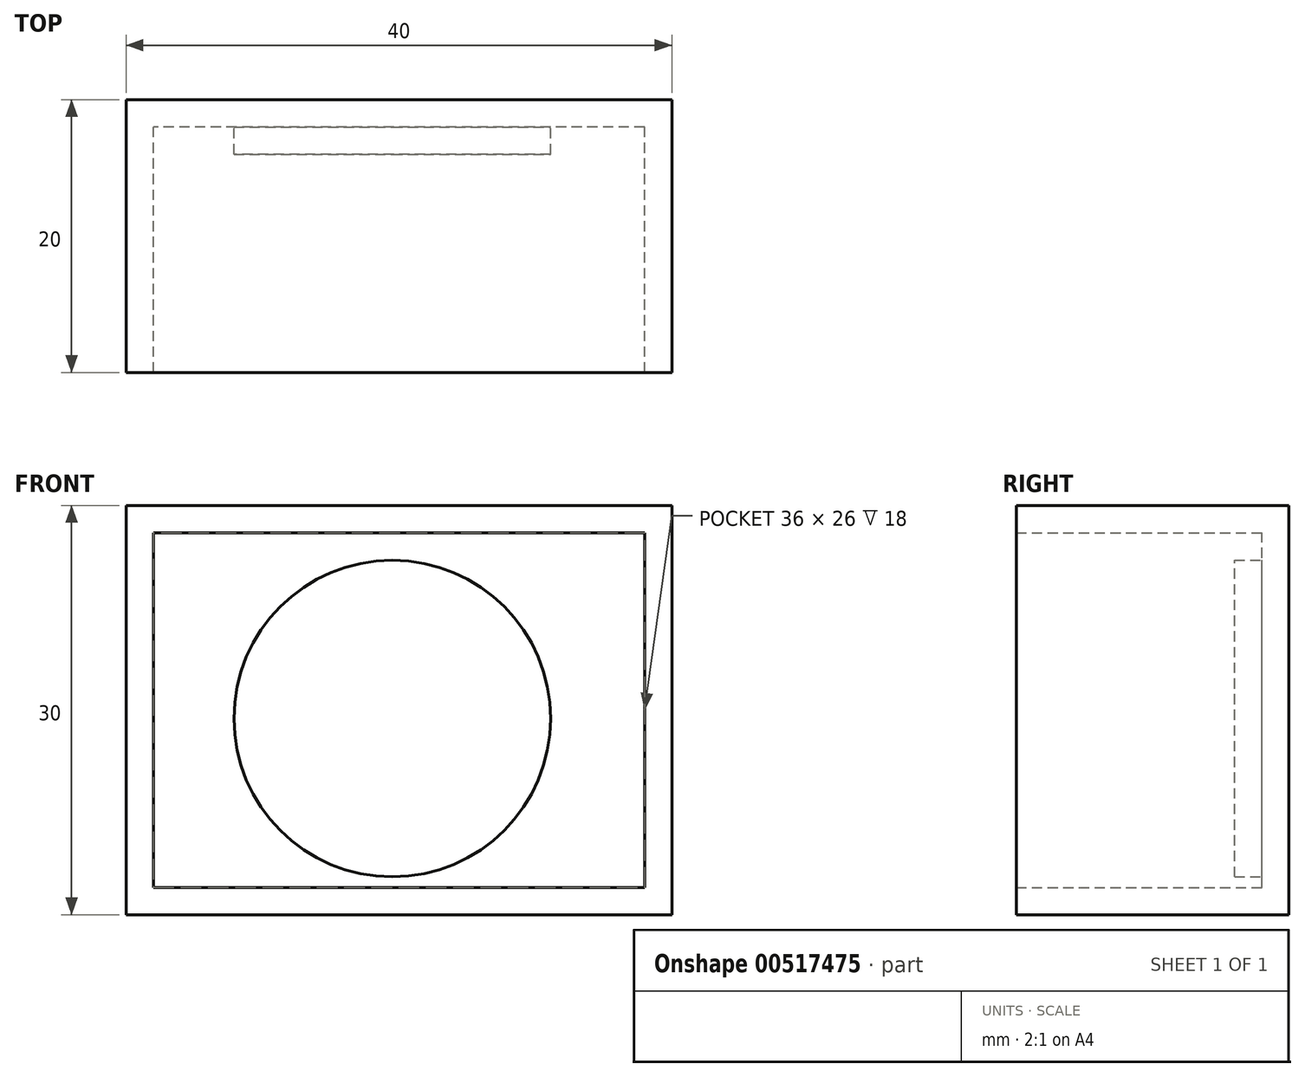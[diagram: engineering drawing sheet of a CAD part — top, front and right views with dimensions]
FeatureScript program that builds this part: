
annotation { "Feature Type Name" : "Feature", "Feature Type Description" : "" }
export const myFeature = defineFeature(function(context is Context, id is Id, definition is map)
    precondition{}
    {
        {
            var Q0;
            Q0=qCreatedBy(makeId("Front.planeOp"),FACE);
            var sketch = newSketch(context, id + "F0", { "sketchPlane" : qUnion([Q0])});
            skLineSegment(sketch, "E0.bottom", {"start": v(0, 0) * mm, "end": v(-40, 0) * mm});
            skLineSegment(sketch, "E0.top", {"start": v(0, 30) * mm, "end": v(-40, 30) * mm});
            skLineSegment(sketch, "E0.left", {"start": v(0, 0) * mm, "end": v(0, 30) * mm});
            skLineSegment(sketch, "E0.right", {"start": v(-40, 0) * mm, "end": v(-40, 30) * mm});
            skSolve(sketch);
        }
        {
            var Q0;
            Q0 = qSketchRegion(id + "F0", true);
            var Q1;
            Q1=makeQuery(id+"F0.imprint","IMPRINT",FACE,{"disambiguationData":[TD([[makeQuery(id+"F0.imprint","IMPRINT",EDGE,{"derivedFrom":sQuery(id+"F0.wireOp",EDGE,"E0.bottom")}),-1.0]])]});
            extrude(context, id + "F1", {"entities" : qUnion([Q0, Q1]), "depth" : 20 * mm, "offsetDistance" : 25.4 * mm});
        }
        {
            var Q0;
            Q0=makeQuery(id+"F1.opExtrude","CAP_FACE",FACE,{"disambiguationData":[OSD([sQuery(id+"F0.wireOp",EDGE,"E0.bottom"),sQuery(id+"F0.wireOp",EDGE,"E0.top"),sQuery(id+"F0.wireOp",EDGE,"E0.left"),sQuery(id+"F0.wireOp",EDGE,"E0.right")])],"isStart":false});
            shell(context, id + "F2", {"entities" : qUnion([Q0]), "thickness" : 2 * mm});
        }
        {
            var Q0;
            Q0=makeQuery(id+"F2.opShell","OFFSET_FACE",FACE,{"disambiguationData":[OSD([sQuery(id+"F0.wireOp",EDGE,"E0.bottom"),sQuery(id+"F0.wireOp",EDGE,"E0.top"),sQuery(id+"F0.wireOp",EDGE,"E0.left"),sQuery(id+"F0.wireOp",EDGE,"E0.right")])]});
            var sketch = newSketch(context, id + "F3", { "sketchPlane" : qUnion([Q0])});
            skCircle(sketch, "E1", {"center": v(-20.5, 14.38) * mm, "radius": 11.6 * mm});
            skSolve(sketch);
        }
        {
            var Q0;
            Q0 = qSketchRegion(id + "F3", true);
            extrude(context, id + "F4", {"entities" : qUnion([Q0]), "depth" : 2 * mm, "offsetDistance" : 25.4 * mm});
        }
        {
            var Q0;
            Q0=makeQuery(id+"F4.opExtrude","CAP_FACE",FACE,{"disambiguationData":[OSD([sQuery(id+"F3.wireOp",EDGE,"E1")])],"isStart":false});
            var sketch = newSketch(context, id + "F5", { "sketchPlane" : qUnion([Q0])});
            skFitSpline(sketch, "E2", {"points": [v(-27.19, 21.69) * mm, v(-18.67, 23.2) * mm, v(-14.08, 18.31) * mm, v(-16.3, 16.87) * mm, v(-17.61, 19.95) * mm, v(-23.39, 20.05) * mm, v(-18.05, 15.5) * mm, v(-11.23, 14.62) * mm, v(-12.76, 8.41) * mm, v(-13.1, 10.87) * mm, v(-19, 12.84) * mm, v(-14.94, 6.38) * mm, v(-21.24, 7.18) * mm, v(-25.85, 10.93) * mm, v(-19.56, 11.43) * mm, v(-22.04, 15.03) * mm, v(-29.02, 11.56) * mm, v(-26.94, 16.08) * mm, v(-25.98, 18.36) * mm, v(-28.16, 17.37) * mm], "startDerivative": vector(126.6, 53.82) * mm, "endDerivative": vector(-81.69, -47.85) * mm});
            skSolve(sketch);
        }
        {
            var Q0;
            Q0 = qBodyType(qCreatedBy(id + "F5" ,EDGE), BodyType.WIRE);
            var Q1;
            Q1=sQuery(id+"F5.wireOp",EDGE,"E2");
            extrude(context, id + "F6", {"bodyType" : ToolBodyType.SURFACE, "surfaceEntities" : qUnion([Q0, Q1]), "depth" : 5 * mm, "offsetDistance" : 25.4 * mm});
        }
    });
